# Revit family: SENT315T
name_source: partatom
category: Mechanical Equipment
revit_build: Autodesk Revit MEP 2013 (Build: 20120221_2030(x64)
units: mm (PartAtom-declared; Revit-internal decimal feet)

## types (1)
- SENT315T
    AC Frequency Input = 50Hz nominal
    AC Voltage Input = 220-240 V AC (single phase)
    Category = Sentinel D-Box Twin Fan
    Country of Manufacture = UK
    Height = 536mm
    IP Rating  External (WP) = IPX5
    IP Rating  Internal = IPX2
    Length (excluding Spigots) = 1255mm
    Length (including Spigots) = 1353mm
    Manufacturer - Name = Vent-Axia Ltd
    Manufacturer - Website = www.vent-axia.com
    Motor Rating = 173 Watts (max)
    Operating Temperature = (-10C to +40C)
    Operational and Maintenance Manual = http://www.vent-axia.com
    Options = Weatherproofed and Constant Pressure options
    Part Number = SENT315T
    Product Description = Sentinel D-Box Twin Fan
    Spigot Diameter = 315mm
    Warranty period = Unit 2 Years                                       Motor 5 Years
    Weight = 88Kg
    Width (excluding controller) = 1176mm
    Width (including controller) = 1272mm

## geometry (parser evidence)
native form markers: Sweep x1
no freeform markers — native parametric forms only
